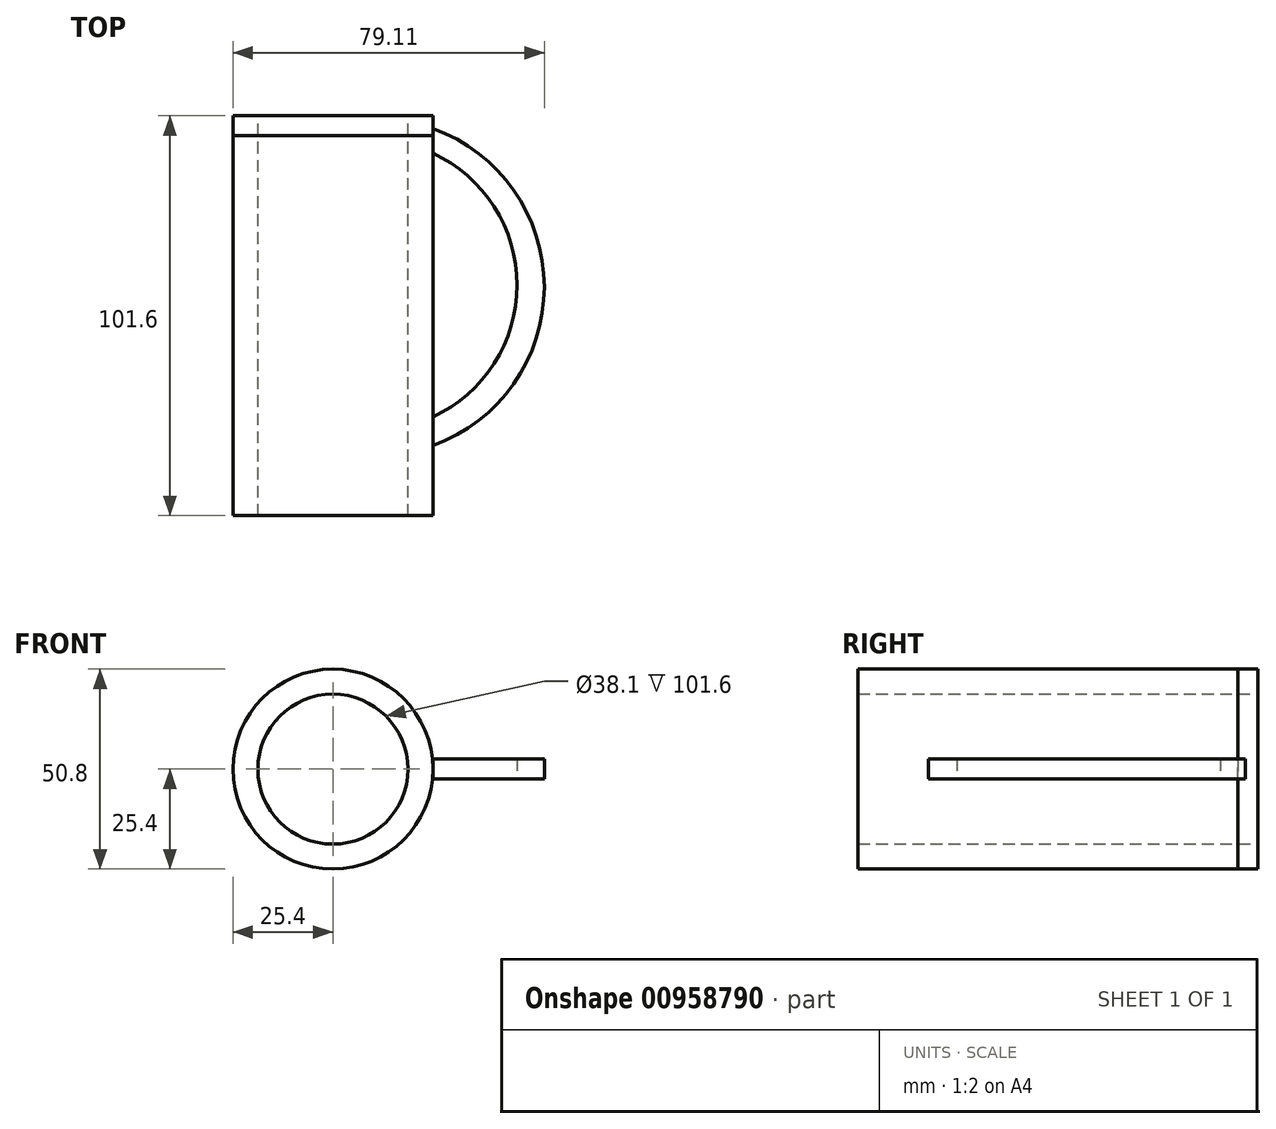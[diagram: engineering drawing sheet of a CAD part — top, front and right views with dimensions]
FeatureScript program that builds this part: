
annotation { "Feature Type Name" : "Feature", "Feature Type Description" : "" }
export const myFeature = defineFeature(function(context is Context, id is Id, definition is map)
    precondition{}
    {
        {
            var Q0;
            Q0=qCreatedBy(makeId("Front.planeOp"),FACE);
            var sketch = newSketch(context, id + "F0", { "sketchPlane" : qUnion([Q0])});
            skCircle(sketch, "E0", {"center": v(0, 0) * mm, "radius": 25.4 * mm});
            skCircle(sketch, "E1", {"center": v(0, 0) * mm, "radius": 19.05 * mm});
            skSolve(sketch);
        }
        {
            var Q0;
            Q0=makeQuery(id+"F0.imprint","IMPRINT",FACE,{"disambiguationData":[TD([[makeQuery(id+"F0.imprint","IMPRINT",EDGE,{"derivedFrom":sQuery(id+"F0.wireOp",EDGE,"E0")}),1.0]])]});
            extrude(context, id + "F1", {"entities" : qUnion([Q0]), "depth" : 101.6 * mm, "offsetDistance" : 25.4 * mm});
        }
        {
            var Q0;
            Q0=qCreatedBy(makeId("Top.planeOp"),FACE);
            var sketch = newSketch(context, id + "F2", { "sketchPlane" : qUnion([Q0])});
            skArc(sketch, "E2", {"start": v(25.08, -83.87) * mm, "mid": v(53.7, -43.5) * mm, "end": v(25.08, -3.11) * mm});
            skArc(sketch, "E3", {"start": v(25.33, -76.58) * mm, "mid": v(46.8, -43.05) * mm, "end": v(25.4, -9.49) * mm});
            skLineSegment(sketch, "E4", {"start": v(25.4, 0) * mm, "end": v(25.4, -101.6) * mm});
            skSolve(sketch);
        }
        {
            var Q0;
            {var subQ0=sQuery(id+"F2.wireOp",EDGE,"E4");var subQ1=sQuery(id+"F2.wireOp",EDGE,"E2");var subQ2=makeQuery(id+"F2.imprint","INTERSECT",VERTEX,{"disambiguationData":[OD(0.0)],"derivedFrom":[subQ1,subQ0]});Q0=makeQuery(id+"F2.imprint","IMPRINT",FACE,{"disambiguationData":[TD([[makeQuery(id+"F2.imprint","IMPRINT",EDGE,{"disambiguationData":[TD([[subQ2,1.0]])],"derivedFrom":subQ1}),1.0]])]});}
            extrude(context, id + "F3", {"entities" : qUnion([Q0]), "depth" : 5.08 * mm, "offsetDistance" : 25.4 * mm, "symmetric" : true});
        }
        {
            var Q0;
            Q0=qCreatedBy(makeId("Front.planeOp"),FACE);
            var sketch = newSketch(context, id + "F4", { "sketchPlane" : qUnion([Q0])});
            skCircle(sketch, "E5", {"center": v(0, 0) * mm, "radius": 25.4 * mm});
            skSolve(sketch);
        }
        {
            var Q0;
            Q0 = qSketchRegion(id + "F4", true);
            extrude(context, id + "F5", {"entities" : qUnion([Q0]), "depth" : 5.08 * mm, "offsetDistance" : 25.4 * mm});
        }
    });
